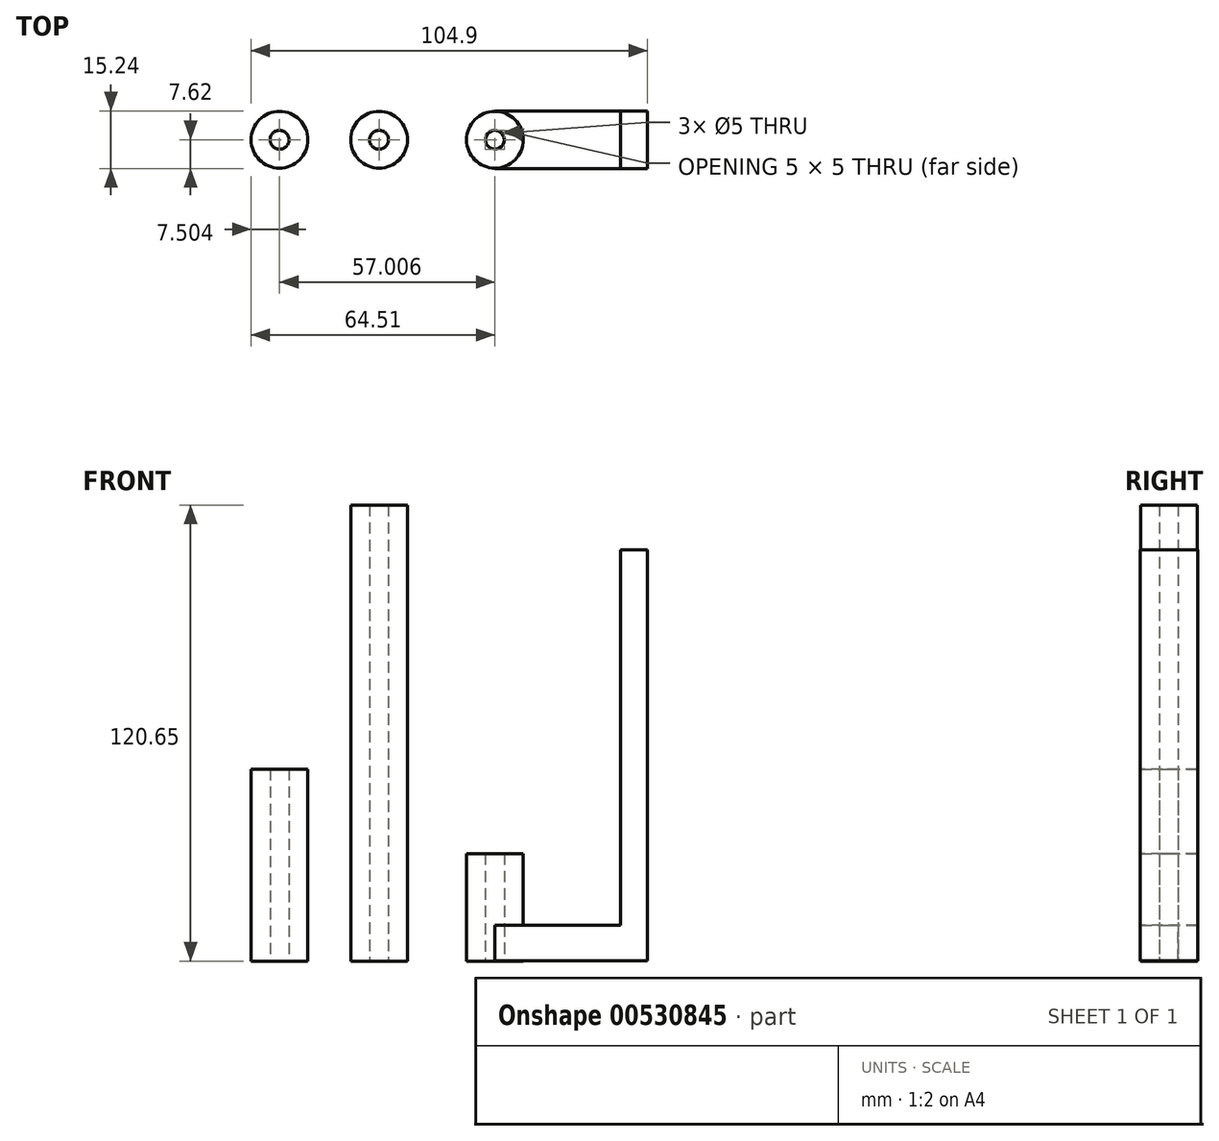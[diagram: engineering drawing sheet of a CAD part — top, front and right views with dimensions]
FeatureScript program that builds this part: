
annotation { "Feature Type Name" : "Feature", "Feature Type Description" : "" }
export const myFeature = defineFeature(function(context is Context, id is Id, definition is map)
    precondition{}
    {
        {
            var Q0;
            Q0=qCreatedBy(makeId("Top.planeOp"),FACE);
            var sketch = newSketch(context, id + "F0", { "sketchPlane" : qUnion([Q0])});
            skCircle(sketch, "E0", {"center": v(-30.65, 0) * mm, "radius": 2.5 * mm});
            skCircle(sketch, "E1", {"center": v(-30.65, 0) * mm, "radius": 7.5 * mm});
            skSolve(sketch);
        }
        {
            var Q0;
            Q0=makeQuery(id+"F0.imprint","IMPRINT",FACE,{"disambiguationData":[TD([[makeQuery(id+"F0.imprint","IMPRINT",EDGE,{"derivedFrom":sQuery(id+"F0.wireOp",EDGE,"E0")}),-1.0]])]});
            var Q1;
            Q1=makeQuery(id+"F0.imprint","IMPRINT",FACE,{"disambiguationData":[TD([[makeQuery(id+"F0.imprint","IMPRINT",EDGE,{"derivedFrom":sQuery(id+"F0.wireOp",EDGE,"eea50cdb-3b6c-40ec-a69c-a4b881eb21f5")}),-1.0]])]});
            var Q2;
            Q2=makeQuery(id+"F0.imprint","IMPRINT",FACE,{"disambiguationData":[TD([[makeQuery(id+"F0.imprint","IMPRINT",EDGE,{"derivedFrom":sQuery(id+"F0.wireOp",EDGE,"e1948dd0-7f1b-4d70-92af-565bf85c3727")}),-1.0]])]});
            var Q3;
            Q3=makeQuery(id+"F0.imprint","IMPRINT",FACE,{"disambiguationData":[TD([[makeQuery(id+"F0.imprint","IMPRINT",EDGE,{"derivedFrom":sQuery(id+"F0.wireOp",EDGE,"fcd34754-d67f-442b-8768-269fce0919a4")}),-1.0]])]});
            extrude(context, id + "F1", {"entities" : qUnion([Q0, Q1, Q2, Q3]), "depth" : 120.65 * mm, "offsetDistance" : 25.4 * mm});
        }
        {
            var Q0;
            Q0=qCreatedBy(makeId("Top.planeOp"),FACE);
            var sketch = newSketch(context, id + "F2", { "sketchPlane" : qUnion([Q0])});
            skCircle(sketch, "E2", {"center": v(0, 0) * mm, "radius": 7.5 * mm});
            skCircle(sketch, "E3", {"center": v(0, 0) * mm, "radius": 2.5 * mm});
            skSolve(sketch);
        }
        {
            var Q0;
            Q0 = qSketchRegion(id + "F2", true);
            extrude(context, id + "F3", {"entities" : qUnion([Q0]), "depth" : 28.45 * mm, "offsetDistance" : 25.4 * mm});
        }
        {
            var Q0;
            Q0=qCreatedBy(makeId("Right.planeOp"),FACE);
            var sketch = newSketch(context, id + "F4", { "sketchPlane" : qUnion([Q0])});
            skLineSegment(sketch, "E4.bottom", {"start": v(-7.62, 9.49) * mm, "end": v(7.62, 9.49) * mm});
            skLineSegment(sketch, "E4.top", {"start": v(-7.62, 0.12) * mm, "end": v(7.62, 0.12) * mm});
            skLineSegment(sketch, "E4.left", {"start": v(-7.62, 9.49) * mm, "end": v(-7.62, 0.12) * mm});
            skLineSegment(sketch, "E4.right", {"start": v(7.62, 9.49) * mm, "end": v(7.62, 0.12) * mm});
            skSolve(sketch);
        }
        {
            var Q0;
            Q0 = qSketchRegion(id + "F4", true);
            extrude(context, id + "F5", {"entities" : qUnion([Q0]), "operationType" : NewBodyOperationType.ADD, "depth" : 40.4 * mm, "offsetDistance" : 25.4 * mm});
        }
        {
            var Q0;
            {var subQ3=sQuery(id+"F4.wireOp",EDGE,"E4.bottom");Q0=makeQuery(id+"F5.boolean.opBoolean","SPLIT",FACE,{"disambiguationData":[TD([makeQuery(id+"F3.opExtrude","SWEPT_FACE",FACE,{"disambiguationData":[OSD([sQuery(id+"F2.wireOp",EDGE,"E2")])]})])],"derivedFrom":makeQuery(id+"F5.opExtrude","SWEPT_FACE",FACE,{"disambiguationData":[OSD([subQ3])]})});}
            var sketch = newSketch(context, id + "F6", { "sketchPlane" : qUnion([Q0])});
            skLineSegment(sketch, "E5.bottom", {"start": v(40.39, 7.62) * mm, "end": v(33.2, 7.62) * mm});
            skLineSegment(sketch, "E5.top", {"start": v(40.39, -7.62) * mm, "end": v(33.2, -7.62) * mm});
            skLineSegment(sketch, "E5.left", {"start": v(40.39, 7.62) * mm, "end": v(40.39, -7.62) * mm});
            skLineSegment(sketch, "E5.right", {"start": v(33.2, 7.62) * mm, "end": v(33.2, -7.62) * mm});
            skSolve(sketch);
        }
        {
            var Q0;
            Q0 = qSketchRegion(id + "F6", true);
            extrude(context, id + "F7", {"entities" : qUnion([Q0]), "operationType" : NewBodyOperationType.ADD, "depth" : 99.31 * mm, "offsetDistance" : 25.4 * mm});
        }
        {
            var Q0;
            Q0=qCreatedBy(makeId("Top.planeOp"),FACE);
            var sketch = newSketch(context, id + "F8", { "sketchPlane" : qUnion([Q0])});
            skCircle(sketch, "E6", {"center": v(0, 0) * mm, "radius": 2.5 * mm});
            skSolve(sketch);
        }
        {
            var Q0;
            Q0 = qSketchRegion(id + "F8", true);
            extrude(context, id + "F9", {"entities" : qUnion([Q0]), "operationType" : NewBodyOperationType.REMOVE, "depth" : 162.8 * mm, "offsetDistance" : 25.4 * mm});
        }
        {
            var Q0;
            Q0=qCreatedBy(makeId("Top.planeOp"),FACE);
            var sketch = newSketch(context, id + "F10", { "sketchPlane" : qUnion([Q0])});
            skCircle(sketch, "E7", {"center": v(-57, 0) * mm, "radius": 7.5 * mm});
            skCircle(sketch, "E8", {"center": v(-57, 0) * mm, "radius": 2.5 * mm});
            skSolve(sketch);
        }
        {
            var Q0;
            Q0 = qSketchRegion(id + "F10", true);
            extrude(context, id + "F11", {"entities" : qUnion([Q0]), "depth" : 50.8 * mm, "offsetDistance" : 25.4 * mm});
        }
    });
